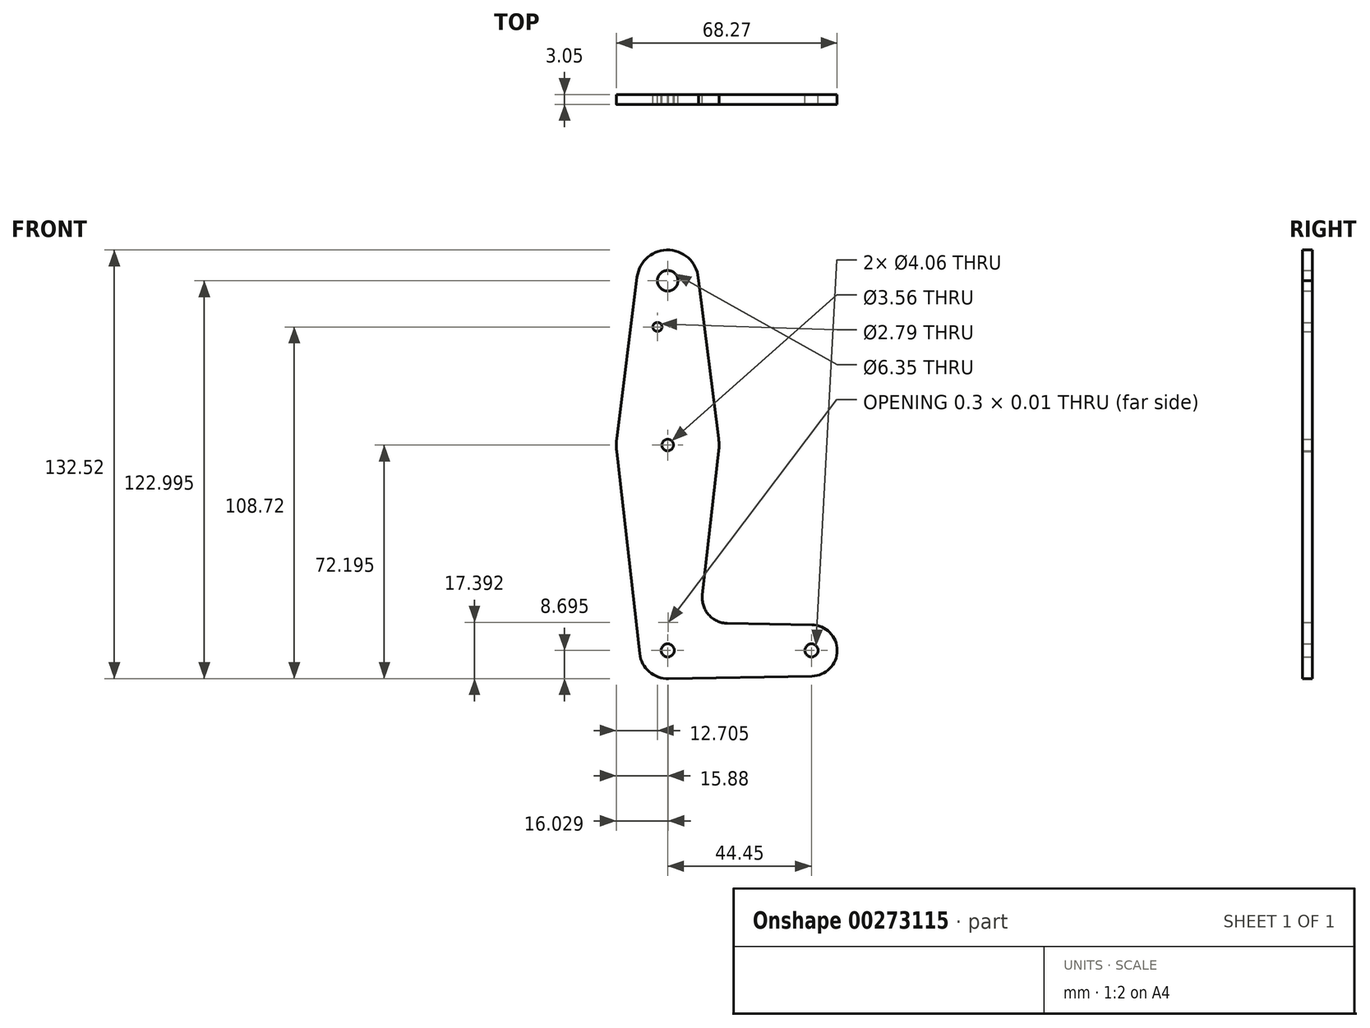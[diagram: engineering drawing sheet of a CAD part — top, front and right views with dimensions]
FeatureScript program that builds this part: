
annotation { "Feature Type Name" : "Feature", "Feature Type Description" : "" }
export const myFeature = defineFeature(function(context is Context, id is Id, definition is map)
    precondition{}
    {
        {
            var Q0;
            Q0=qCreatedBy(makeId("Front.planeOp"),FACE);
            var sketch = newSketch(context, id + "F0", { "sketchPlane" : qUnion([Q0])});
            skCircle(sketch, "E0", {"center": v(0, 66.68) * mm, "radius": 9.53 * mm});
            skCircle(sketch, "E1", {"center": v(0, 15.88) * mm, "radius": 15.88 * mm});
            skCircle(sketch, "E2", {"center": v(0, -47.63) * mm, "radius": 8.7 * mm});
            skCircle(sketch, "E3", {"center": v(44.45, -47.62) * mm, "radius": 7.94 * mm});
            skLineSegment(sketch, "E4", {"start": v(0, 66.68) * mm, "end": v(0, -47.63) * mm});
            skLineSegment(sketch, "E5", {"start": v(0, -47.63) * mm, "end": v(44.45, -47.62) * mm});
            skLineSegment(sketch, "E6", {"start": v(-9.45, 67.87) * mm, "end": v(-15.75, 17.86) * mm});
            skCircle(sketch, "E7", {"center": v(0, 66.68) * mm, "radius": 3.18 * mm});
            skCircle(sketch, "E8", {"center": v(0, 15.88) * mm, "radius": 1.78 * mm});
            skCircle(sketch, "E9", {"center": v(0, -47.63) * mm, "radius": 2.03 * mm});
            skCircle(sketch, "E10", {"center": v(44.45, -47.62) * mm, "radius": 2.03 * mm});
            skCircle(sketch, "E11", {"center": v(-3.17, 52.4) * mm, "radius": 1.4 * mm});
            skLineSegment(sketch, "E12", {"start": v(9.52, 66.68) * mm, "end": v(15.75, 17.88) * mm});
            skLineSegment(sketch, "E13", {"start": v(0, -56.32) * mm, "end": v(44.59, -55.56) * mm});
            skLineSegment(sketch, "E14", {"start": v(15.77, 14.08) * mm, "end": v(10.72, -30.4) * mm});
            skLineSegment(sketch, "E15", {"start": v(-15.75, 13.9) * mm, "end": v(-8.64, -48.6) * mm});
            skLineSegment(sketch, "E16", {"start": v(0, -38.93) * mm, "end": v(0.3, -38.93) * mm});
            skLineSegment(sketch, "E17.trimOffspring", {"start": v(18.48, -39.24) * mm, "end": v(44.59, -39.69) * mm});
            skArc(sketch, "E18.filletArc", {"start": v(10.72, -30.4) * mm, "mid": v(12.64, -36.54) * mm, "end": v(18.48, -39.24) * mm});
            skSolve(sketch);
        }
        {
            var Q0;
            Q0 = qSketchRegion(id + "F0", true);
            var Q1;
            {var subQ5=sQuery(id+"F0.wireOp",EDGE,"E16");Q1=makeQuery(id+"F0.imprint","IMPRINT",FACE,{"disambiguationData":[TD([[makeQuery(id+"F0.imprint","IMPRINT",EDGE,{"derivedFrom":subQ5}),-1.0]])]});}
            extrude(context, id + "F1", {"entities" : qUnion([Q0, Q1]), "depth" : 3.05 * mm});
        }
    });
